# Revit family: Basketball_Backstop-Wall_Mount-Fold-IPIbyBison-IP15WSF
name_source: partatom
category: Specialty Equipment
units: mm (PartAtom-declared; Revit-internal decimal feet)

## family parameters
Always vertical = No
Cut with Voids When Loaded = No
Enable Cutting in Views = No
Maintain Annotation Orientation = No
OmniClass Number = 23.40.50.34.14
OmniClass Title = Gymnasium Equipment
Part Type = Normal
Room Calculation Point = No
Round Connector Dimension = Use Diameter
Shared = No
Work Plane-Based = Yes

## types (2) — shared parameters
CAD Details = https://www.arcat.com
Default Elevation = 0' - 0"
Description = Basketball Frame and Backboard, Wall Mount
Keynote = 11 66 00
Manufacturer = IPI by Bison
Model = IP15WSF Right
Product Page URL = https://www.arcat.com
Specification = https://www.arcat.com
URL = https://ipibybison.com
Unit Depth = 2' - 8"
Unit Width = 7' - 0"
Wall Plate Material = Wood- IPI by Bison
wall distance text = 4 to 10 ft from Wall

## per-type parameters (varying)
| type | Fold Left | Fold Right |
| Wall Mounted Fold Right | No | Yes |
| Wall Mounted Fold Left | Yes | No |

## geometry (parser evidence)
native form markers: Sweep x5
no freeform markers — native parametric forms only
